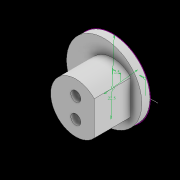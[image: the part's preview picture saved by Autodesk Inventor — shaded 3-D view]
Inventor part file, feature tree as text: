
AUTODESK INVENTOR PART (.ipt)
format: ipt  version: 2022.2 (Build 262287010, 287A)  size: 117,248 bytes
history: native  units: mm
features: sketch x3, extrude x3, hole x1, draft x1, plane x1
ambient origin geometry x8: Origin, YZ Plane, XZ Plane, XY Plane, X Axis, Y Axis, Z Axis, Center Point
bodies: Solid1 (feature_tree)
feature tree (9):
  sketch  "Sketch1"  dims[d0=22.5mm d1=2.5mm]
  extrude  "Extrusion1"  Depth=2.5mm
  extrude  "Extrusion2"  Depth=2.0mm
  hole  "Hole1"  [1 undecoded]
  draft  "FaceDraft1"
  plane  "Work Plane1"
  extrude  "Extrusion3"  Depth=4.0mm
  sketch  "Sketch2"  dims[d2=15.0mm d3=2.0mm]
  sketch  "Sketch3"  dims[d4=2.5mm d5=0.0mm d6=11.0mm d7=0.0mm d8=3.0mm d10=3.0mm d11=6.0mm d12=4.0mm d13=2.0mm d14=90.0deg d15=4.0mm d16=0.0mm d17=20.0mm d18=25.0mm d19=25.0mm d20=2.0mm d21=0.0mm d22=0.436332mm d23=5.5mm]
note: 1 required parameter value undecoded (feature->parameter linkage not recoverable at this tier; creation-order binding heuristic only, values carry confidence <= 0.55)
